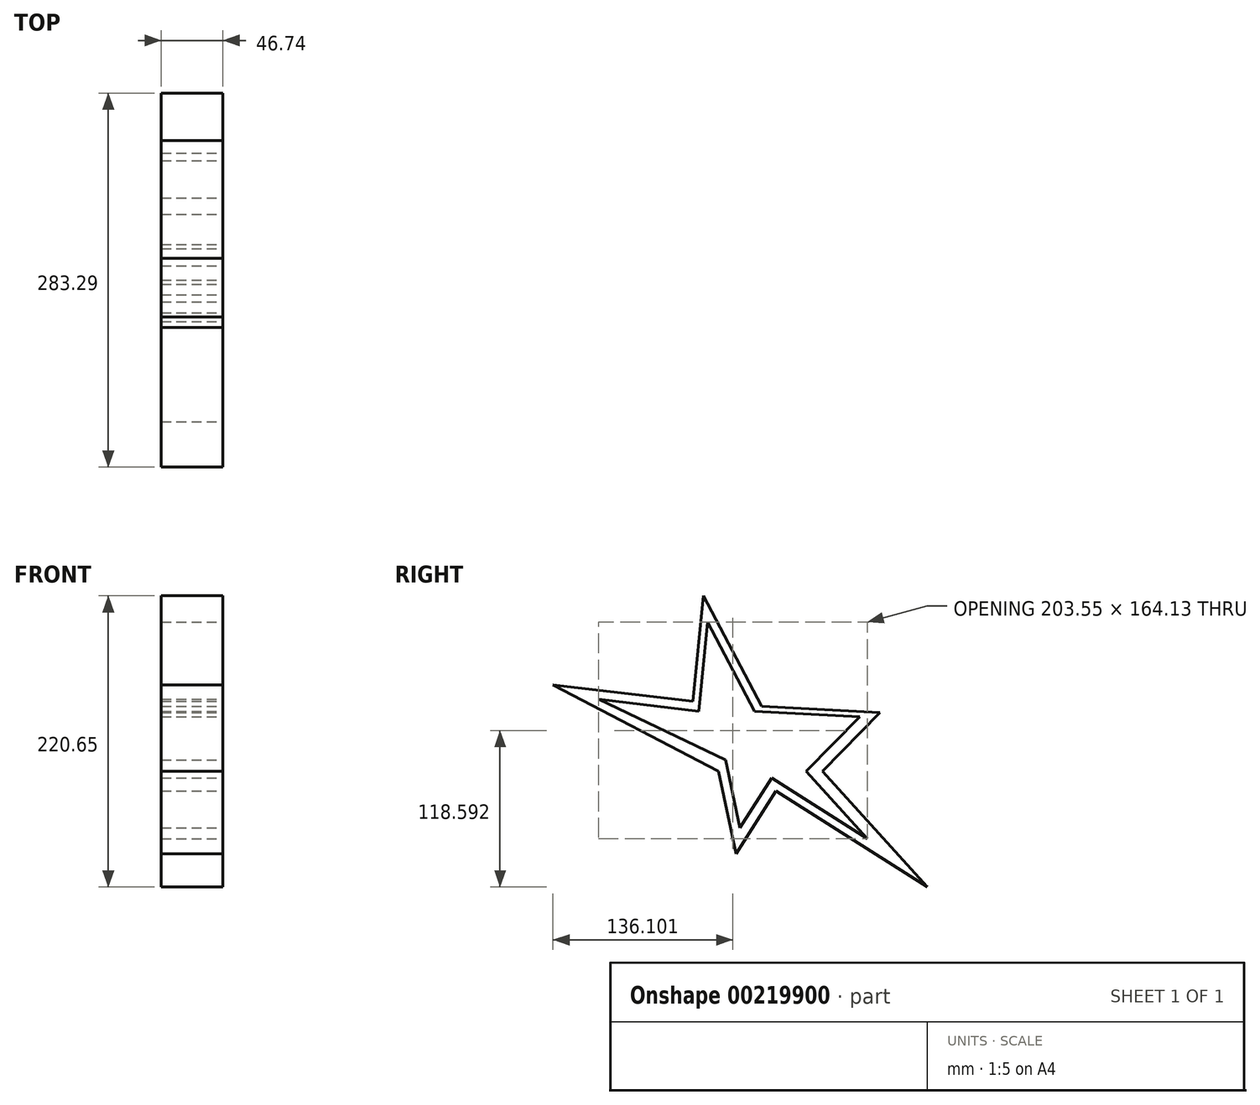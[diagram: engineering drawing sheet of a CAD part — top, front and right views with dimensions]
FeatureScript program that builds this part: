
annotation { "Feature Type Name" : "Feature", "Feature Type Description" : "" }
export const myFeature = defineFeature(function(context is Context, id is Id, definition is map)
    precondition{}
    {
        {
            var Q0;
            Q0=qCreatedBy(makeId("Right.planeOp"),FACE);
            var sketch = newSketch(context, id + "F0", { "sketchPlane" : qUnion([Q0])});
            skLineSegment(sketch, "E0", {"start": v(-19.32, 34.65) * mm, "end": v(-11.45, 114.55) * mm});
            skLineSegment(sketch, "E1", {"start": v(-11.45, 114.55) * mm, "end": v(32.9, 30.84) * mm});
            skLineSegment(sketch, "E2", {"start": v(32.9, 30.84) * mm, "end": v(122.33, 26.19) * mm});
            skLineSegment(sketch, "E3", {"start": v(122.33, 26.19) * mm, "end": v(78.7, -18.49) * mm});
            skLineSegment(sketch, "E4", {"start": v(78.7, -18.49) * mm, "end": v(158.1, -106.1) * mm});
            skLineSegment(sketch, "E5", {"start": v(158.1, -106.1) * mm, "end": v(43.64, -33.18) * mm});
            skLineSegment(sketch, "E6", {"start": v(43.64, -33.18) * mm, "end": v(13.28, -80.83) * mm});
            skLineSegment(sketch, "E7", {"start": v(13.28, -80.83) * mm, "end": v(0, -18.49) * mm});
            skLineSegment(sketch, "E8", {"start": v(0, -18.49) * mm, "end": v(-125.2, 47.1) * mm});
            skLineSegment(sketch, "E9", {"start": v(-125.2, 47.1) * mm, "end": v(-19.32, 34.65) * mm});
            skSolve(sketch);
        }
        {
            var Q0;
            Q0 = qSketchRegion(id + "F0", true);
            extrude(context, id + "F1", {"entities" : qUnion([Q0]), "oppositeDirection" : true, "depth" : 46.74 * mm});
        }
        {
            var Q0;
            Q0=makeQuery(id+"F1.opExtrude","CAP_FACE",FACE,{"disambiguationData":[OSD([sQuery(id+"F0.wireOp",EDGE,"E0"),sQuery(id+"F0.wireOp",EDGE,"E1"),sQuery(id+"F0.wireOp",EDGE,"E2"),sQuery(id+"F0.wireOp",EDGE,"E3"),sQuery(id+"F0.wireOp",EDGE,"E4"),sQuery(id+"F0.wireOp",EDGE,"E5"),sQuery(id+"F0.wireOp",EDGE,"E6"),sQuery(id+"F0.wireOp",EDGE,"E7"),sQuery(id+"F0.wireOp",EDGE,"E8"),sQuery(id+"F0.wireOp",EDGE,"E9")])],"isStart":true});
            var sketch = newSketch(context, id + "F2", { "sketchPlane" : qUnion([Q0])});
            skLineSegment(sketch, "E10", {"start": v(-90.87, 36.15) * mm, "end": v(-14.85, 27.2) * mm});
            skLineSegment(sketch, "E11", {"start": v(-14.85, 27.2) * mm, "end": v(-8.21, 94.56) * mm});
            skLineSegment(sketch, "E12", {"start": v(-8.21, 94.56) * mm, "end": v(27.47, 27.2) * mm});
            skLineSegment(sketch, "E13", {"start": v(27.47, 27.2) * mm, "end": v(106.98, 23.07) * mm});
            skLineSegment(sketch, "E14", {"start": v(106.98, 23.07) * mm, "end": v(66.39, -18.49) * mm});
            skLineSegment(sketch, "E15", {"start": v(66.39, -18.49) * mm, "end": v(112.69, -69.57) * mm});
            skLineSegment(sketch, "E16", {"start": v(112.69, -69.57) * mm, "end": v(40.33, -23.47) * mm});
            skLineSegment(sketch, "E17", {"start": v(40.33, -23.47) * mm, "end": v(16.38, -61.06) * mm});
            skLineSegment(sketch, "E18", {"start": v(16.38, -61.06) * mm, "end": v(5.44, -9.7) * mm});
            skLineSegment(sketch, "E19", {"start": v(5.44, -9.7) * mm, "end": v(-90.87, 36.15) * mm});
            skSolve(sketch);
        }
        {
            var Q0;
            Q0 = qSketchRegion(id + "F2", true);
            extrude(context, id + "F3", {"entities" : qUnion([Q0]), "operationType" : NewBodyOperationType.REMOVE, "oppositeDirection" : true, "depth" : 103.12 * mm});
        }
    });
